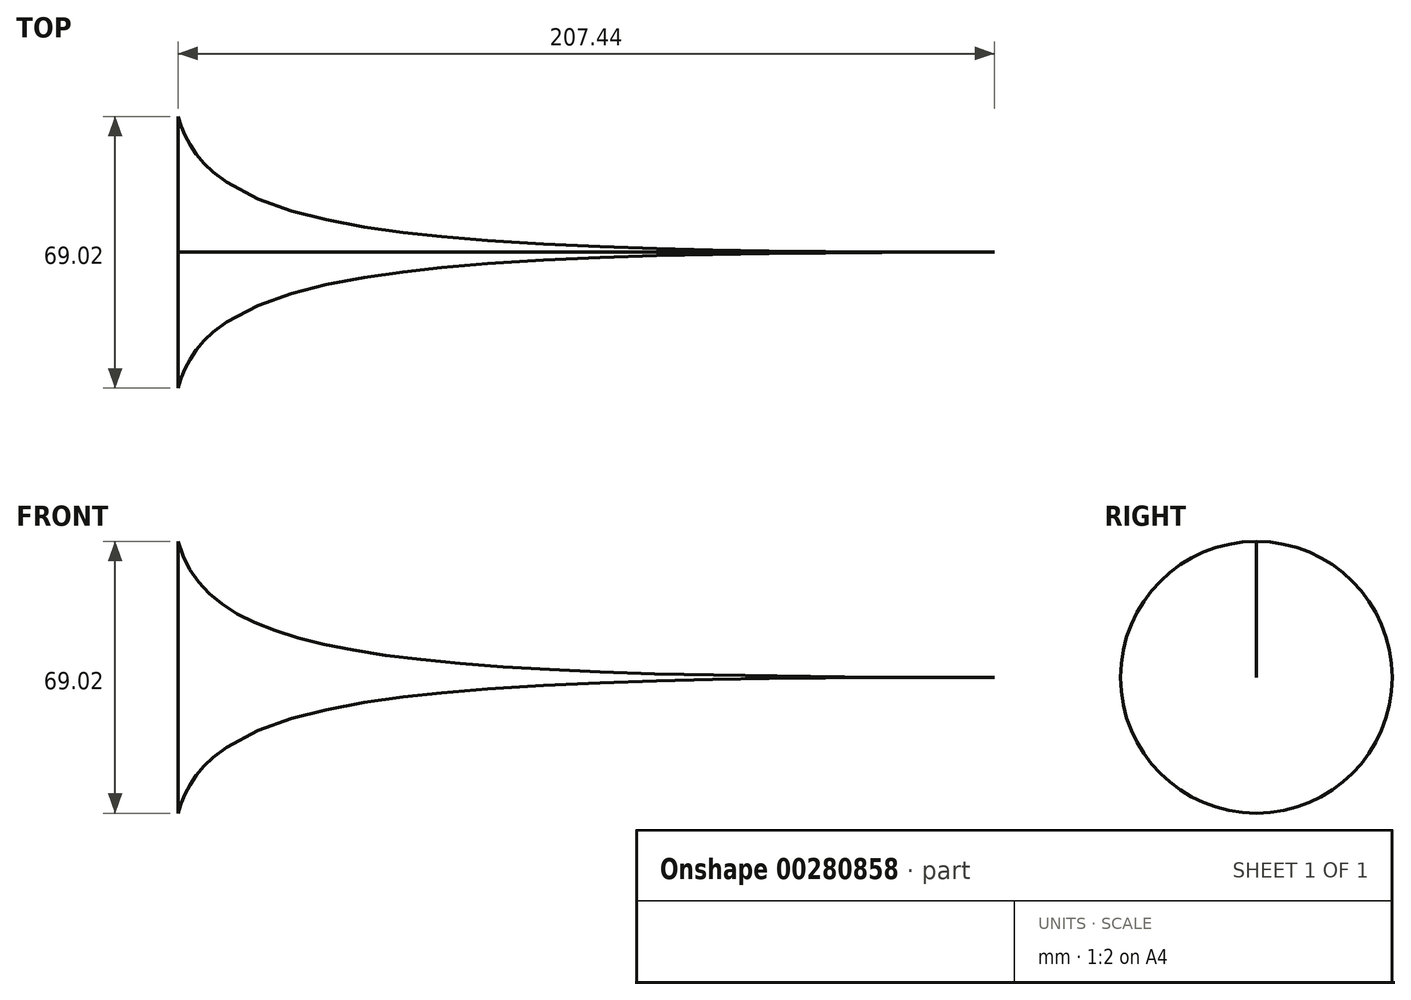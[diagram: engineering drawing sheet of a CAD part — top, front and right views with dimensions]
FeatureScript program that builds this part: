
annotation { "Feature Type Name" : "Feature", "Feature Type Description" : "" }
export const myFeature = defineFeature(function(context is Context, id is Id, definition is map)
    precondition{}
    {
        {
            var Q0;
            Q0=qCreatedBy(makeId("Front.planeOp"),FACE);
            var sketch = newSketch(context, id + "F0", { "sketchPlane" : qUnion([Q0])});
            skFitSpline(sketch, "E0", {"points": [v(0, 34.5) * mm, v(207.44, 0) * mm], "startDerivative": vector(24.37, -88.07) * mm, "endDerivative": vector(466.44, 0) * mm});
            skLineSegment(sketch, "E1", {"start": v(14.34, 0) * mm, "end": v(35.35, 0) * mm, "construction": true});
            skSolve(sketch);
        }
        {
            var Q0;
            Q0=sQuery(id+"F0.wireOp",EDGE,"E0");
            var Q1;
            Q1=sQuery(id+"F0.wireOp",EDGE,"E1");
            revolve(context, id + "F1", {"bodyType" : ToolBodyType.SURFACE, "surfaceEntities" : qUnion([Q0]), "axis" : qUnion([Q1]), "revolveType" : RevolveType.FULL});
        }
    });
